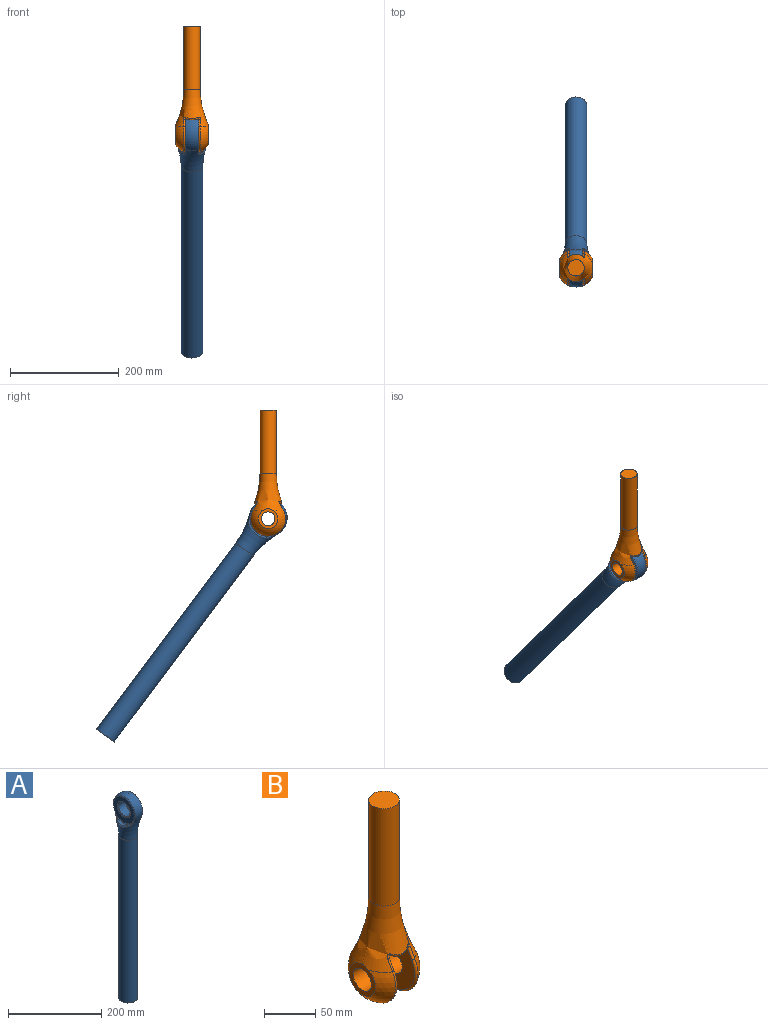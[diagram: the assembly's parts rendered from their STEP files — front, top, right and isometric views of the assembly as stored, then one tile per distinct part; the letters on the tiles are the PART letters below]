
ASSEMBLY  parts=2 mates=1
PART A: 25 faces, bbox 137.5x137.5x536 mm
  f0: sphere r=35mm, area 3093.1mm2, adj f1,f17,f24
  f1: torus R=170mm, axis (0,0,-1), area 6293.1mm2, adj f0,f3,f12,f13,f14,f15,f16,f18
  f2: plane 40x40mm, normal (0,0,-1), area 1256.6mm2, adj f3
  f3: cylinder r=20mm len=427.03mm, axis (0,0,-1), area 53661.8mm2, adj f1,f2
  f4: cylinder r=35mm len=35.33mm, axis (1,0,0), area 196mm2, adj f18,f19
  f5: plane 64.29x62.57mm, normal (-1,0,0), area 1984mm2, adj f9,f19,f22,f23,f24
  f6: plane 64.29x62.57mm, normal (1,0,0), area 1984mm2, adj f10,f11,f15,f16,f17
  f7: cylinder r=35mm len=35.33mm, axis (1,0,0), area 196mm2, adj f11,f12
  f8: cylinder r=17.5mm len=35mm, axis (1,0,0), area 2309.1mm2, adj f9,f10
  f9: torus R=19.5mm, axis (-1,0,0), area 359.8mm2, adj f5,f8
  f10: torus R=19.5mm, axis (-1,0,0), area 359.8mm2, adj f6,f8
  f11: torus R=33mm, axis (-1,0,0), area 147.7mm2, adj f6,f7,f13,f14
  f12: bspline ~42.35x11.62mm, area 173.8mm2, adj f1,f7,f13,f14
  f13: bspline ~15.49x11.28mm, area 39.5mm2, adj f1,f11,f12,f15
  f14: bspline ~13.13x10.52mm, area 39.5mm2, adj f1,f11,f12,f16
  f15: bspline ~25.63x13.26mm, area 23.3mm2, adj f1,f6,f13,f17
  f16: bspline ~25.63x13.26mm, area 23.3mm2, adj f1,f6,f14,f17
  f17: torus R=31.28mm, axis (-1,0,0), area 323mm2, adj f0,f6,f15,f16
  f18: bspline ~43.1x12.17mm, area 173.8mm2, adj f1,f4,f20,f21
  f19: torus R=33mm, axis (-1,0,0), area 147.7mm2, adj f4,f5,f20,f21
  f20: bspline ~13.13x10.52mm, area 39.5mm2, adj f1,f18,f19,f22
  f21: bspline ~15.49x11.28mm, area 39.5mm2, adj f1,f18,f19,f23
  f22: bspline ~25.63x13.26mm, area 23.3mm2, adj f1,f5,f20,f24
  f23: bspline ~25.63x13.26mm, area 23.3mm2, adj f1,f5,f21,f24
  f24: torus R=31.28mm, axis (-1,0,0), area 323mm2, adj f0,f5,f22,f23
PART B: 26 faces, bbox 128x128x235.6 mm
  f0: torus R=165mm, axis (0,0,-1), area 7885.8mm2, adj f1,f2,f4,f5,f6,f10,f11,f12
  f1: sphere r=35mm, area 2303.1mm2, adj f0,f6,f15
  f2: sphere r=35mm, area 2303.1mm2, adj f0,f5,f14
  f3: plane 30x30mm, normal (0,0,1), area 706.9mm2, adj f4
  f4: cylinder r=15mm len=116.33mm, axis (0,0,-1), area 10964.2mm2, adj f0,f3
  f5: plane 36.32x36.06mm, normal (1,0,0), area 532.5mm2, adj f0,f2,f24
  f6: plane 37.64x37.37mm, normal (-1,0,0), area 532.5mm2, adj f0,f1,f25
  f7: cylinder r=35mm len=44mm, axis (1,0,0), area 911.3mm2, adj f10,f17,f20,f23
  f8: plane 62.64x59.29mm, normal (1,0,0), area 2427.8mm2, adj f12,f15,f19,f20,f25
  f9: plane 62.64x59.29mm, normal (-1,0,0), area 2427.8mm2, adj f11,f14,f17,f18,f24
  f10: bspline ~29.92x10.19mm, area 128mm2, adj f0,f7,f13,f16
  f11: bspline ~28.23x17.59mm, area 56.6mm2, adj f0,f9,f13,f14
  f12: bspline ~28.23x17.59mm, area 56.6mm2, adj f0,f8,f15,f16
  f13: bspline ~7.19x6.68mm, area 24.2mm2, adj f0,f10,f11,f17
  f14: torus R=29.64mm, axis (1,0,0), area 528.2mm2, adj f2,f9,f11,f18
  f15: torus R=29.64mm, axis (1,0,0), area 528.2mm2, adj f1,f8,f12,f19
  f16: bspline ~7.15x6.65mm, area 24.2mm2, adj f0,f10,f12,f20
  f17: torus R=33mm, axis (1,0,0), area 118mm2, adj f7,f9,f13,f21
  f18: bspline ~28.23x17.59mm, area 56.6mm2, adj f0,f9,f14,f21
  f19: bspline ~28.23x17.59mm, area 56.6mm2, adj f0,f8,f15,f22
  f20: torus R=33mm, axis (1,0,0), area 117.9mm2, adj f7,f8,f16,f22
  f21: bspline ~7.15x6.65mm, area 24.2mm2, adj f0,f17,f18,f23
  f22: bspline ~7.19x6.68mm, area 24.2mm2, adj f0,f19,f20,f23
  f23: bspline ~29.92x10.19mm, area 128mm2, adj f0,f7,f21,f22
  f24: cylinder r=12.5mm len=25mm, axis (-1,0,0), area 1374.4mm2, adj f5,f9
  f25: cylinder r=12.5mm len=25mm, axis (-1,0,0), area 1374.4mm2, adj f6,f8
PLACE A rot(axis=(0,0.32,-0.95),180deg) t=(0,0,1.84)mm
PLACE B at identity fixed
MATE revolute B.f9 <-> A.f4  axis (-1,0,0) through (12.5,0,1.84)mm
